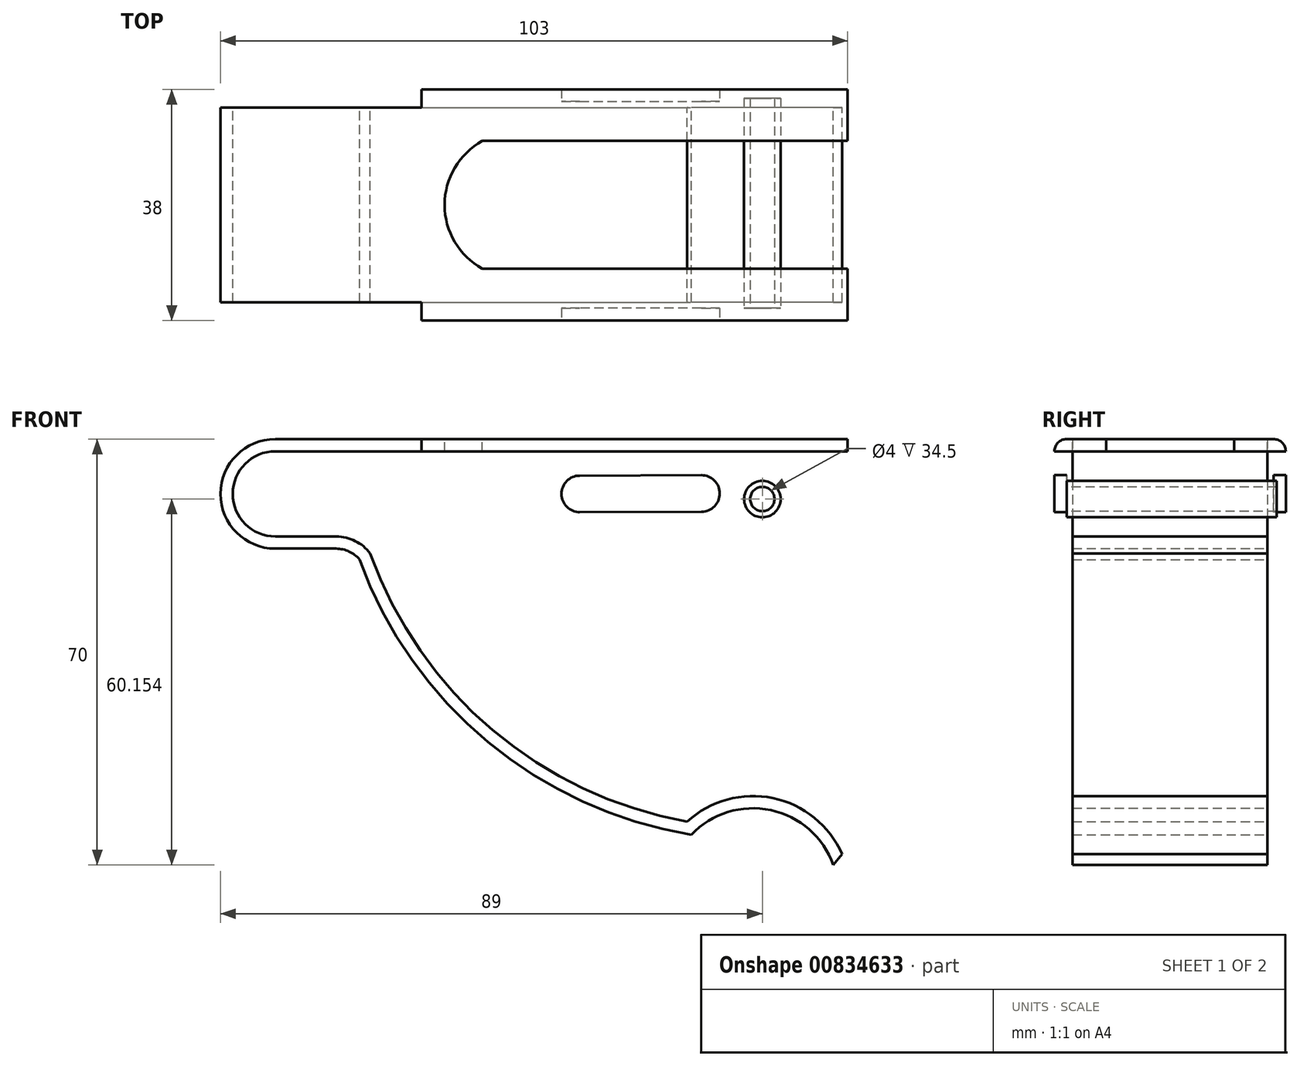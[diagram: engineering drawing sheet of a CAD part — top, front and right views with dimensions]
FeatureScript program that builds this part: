
annotation { "Feature Type Name" : "Feature", "Feature Type Description" : "" }
export const myFeature = defineFeature(function(context is Context, id is Id, definition is map)
    precondition{}
    {
        {
            var Q0;
            Q0=qCreatedBy(makeId("Front.planeOp"),FACE);
            var sketch = newSketch(context, id + "F0", { "sketchPlane" : qUnion([Q0])});
            skArc(sketch, "E0", {"start": v(0, 9) * mm, "mid": v(-9, 0) * mm, "end": v(0, -9) * mm});
            skLineSegment(sketch, "E1", {"start": v(0, 9) * mm, "end": v(94, 9) * mm});
            skLineSegment(sketch, "E2", {"start": v(0, -9) * mm, "end": v(10, -9) * mm});
            skArc(sketch, "E3", {"start": v(13.83, -10.78) * mm, "mid": v(12.1, -9.47) * mm, "end": v(10, -9) * mm});
            skArc(sketch, "E4", {"start": v(13.83, -10.78) * mm, "mid": v(34.94, -40.8) * mm, "end": v(68.33, -56) * mm});
            skArc(sketch, "E5", {"start": v(91.66, -61) * mm, "mid": v(81.4, -51.97) * mm, "end": v(68.33, -56) * mm});
            skLineSegment(sketch, "E6.0", {"start": v(0, 7) * mm, "end": v(94, 7) * mm});
            skArc(sketch, "E6.1", {"start": v(0, 7) * mm, "mid": v(-7, 0) * mm, "end": v(0, -7) * mm});
            skArc(sketch, "E6.2", {"start": v(93.1, -59.22) * mm, "mid": v(81.76, -50) * mm, "end": v(67.66, -53.86) * mm});
            skArc(sketch, "E6.3", {"start": v(15.6, -9.8) * mm, "mid": v(35.7, -38.83) * mm, "end": v(67.66, -53.86) * mm});
            skArc(sketch, "E6.4", {"start": v(15.6, -9.8) * mm, "mid": v(13.13, -7.74) * mm, "end": v(10, -7) * mm});
            skLineSegment(sketch, "E6.5", {"start": v(0, -7) * mm, "end": v(10, -7) * mm});
            skLineSegment(sketch, "E7", {"start": v(91.66, -61) * mm, "end": v(93.1, -59.22) * mm});
            skLineSegment(sketch, "E8", {"start": v(94, 7) * mm, "end": v(94, 9) * mm});
            skSolve(sketch);
        }
        {
            var Q0;
            Q0=makeQuery(id+"F0.imprint","IMPRINT",FACE,{"disambiguationData":[TD([[makeQuery(id+"F0.imprint","IMPRINT",EDGE,{"derivedFrom":sQuery(id+"F0.wireOp",EDGE,"E0")}),1.0]])]});
            extrude(context, id + "F1", {"entities" : qUnion([Q0]), "depth" : 16 * mm, "offsetDistance" : 25 * mm});
        }
        {
            var Q0;
            Q0=makeQuery(id+"F1.opExtrude","SWEPT_FACE",FACE,{"disambiguationData":[OSD([sQuery(id+"F0.wireOp",EDGE,"E1")])]});
            var sketch = newSketch(context, id + "F2", { "sketchPlane" : qUnion([Q0])});
            skLineSegment(sketch, "E9.bottom", {"start": v(94, -16) * mm, "end": v(24, -16) * mm});
            skLineSegment(sketch, "E9.top", {"start": v(94, -19) * mm, "end": v(24, -19) * mm});
            skLineSegment(sketch, "E9.left", {"start": v(94, -16) * mm, "end": v(94, -19) * mm});
            skLineSegment(sketch, "E9.right", {"start": v(24, -16) * mm, "end": v(24, -19) * mm});
            skSolve(sketch);
        }
        {
            var Q0;
            Q0=makeQuery(id+"F2.imprint","IMPRINT",FACE,{"disambiguationData":[TD([[makeQuery(id+"F2.imprint","IMPRINT",EDGE,{"derivedFrom":sQuery(id+"F2.wireOp",EDGE,"E9.bottom")}),-1.0]])]});
            extrude(context, id + "F3", {"entities" : qUnion([Q0]), "operationType" : NewBodyOperationType.ADD, "oppositeDirection" : true, "depth" : 2 * mm, "offsetDistance" : 25 * mm});
        }
        {
            var Q0;
            Q0=makeQuery(id+"F3.opExtrude","SWEPT_FACE",FACE,{"disambiguationData":[OSD([sQuery(id+"F2.wireOp",EDGE,"E9.top")])]});
            var sketch = newSketch(context, id + "F4", { "sketchPlane" : qUnion([Q0])});
            skLineSegment(sketch, "E10.bottom", {"start": v(41.55, 9) * mm, "end": v(94, 9) * mm});
            skLineSegment(sketch, "E10.top", {"start": v(41.55, -6.85) * mm, "end": v(94, -6.85) * mm});
            skLineSegment(sketch, "E10.left", {"start": v(41.55, 9) * mm, "end": v(41.55, -6.85) * mm});
            skLineSegment(sketch, "E10.right", {"start": v(94, 9) * mm, "end": v(94, -6.85) * mm});
            skSolve(sketch);
        }
        {
            var Q0;
            {var subQ0=sQuery(id+"F4.wireOp",EDGE,"E10.top");Q0=makeQuery(id+"F4.imprint","IMPRINT",FACE,{"disambiguationData":[TD([[makeQuery(id+"F4.imprint","IMPRINT",EDGE,{"derivedFrom":subQ0}),1.0]])]});}
            extrude(context, id + "F5", {"entities" : qUnion([Q0]), "operationType" : NewBodyOperationType.ADD, "oppositeDirection" : true, "depth" : 2 * mm, "offsetDistance" : 25 * mm});
        }
        {
            var Q0;
            Q0=makeQuery(id+"F1.opExtrude","SWEPT_BODY",BODY,{"disambiguationData":[OSD([sQuery(id+"F0.wireOp",EDGE,"E0"),sQuery(id+"F0.wireOp",EDGE,"E1"),sQuery(id+"F0.wireOp",EDGE,"E2"),sQuery(id+"F0.wireOp",EDGE,"E3"),sQuery(id+"F0.wireOp",EDGE,"E4"),sQuery(id+"F0.wireOp",EDGE,"E5"),sQuery(id+"F0.wireOp",EDGE,"E6.0"),sQuery(id+"F0.wireOp",EDGE,"E6.1"),sQuery(id+"F0.wireOp",EDGE,"E6.2"),sQuery(id+"F0.wireOp",EDGE,"E6.3"),sQuery(id+"F0.wireOp",EDGE,"E6.4"),sQuery(id+"F0.wireOp",EDGE,"E6.5"),sQuery(id+"F0.wireOp",EDGE,"E7"),sQuery(id+"F0.wireOp",EDGE,"E8")])]});
            var Q1;
            Q1=makeQuery(id+"F1.opExtrude","CAP_FACE",FACE,{"disambiguationData":[OSD([sQuery(id+"F0.wireOp",EDGE,"E0"),sQuery(id+"F0.wireOp",EDGE,"E1"),sQuery(id+"F0.wireOp",EDGE,"E2"),sQuery(id+"F0.wireOp",EDGE,"E3"),sQuery(id+"F0.wireOp",EDGE,"E4"),sQuery(id+"F0.wireOp",EDGE,"E5"),sQuery(id+"F0.wireOp",EDGE,"E6.0"),sQuery(id+"F0.wireOp",EDGE,"E6.1"),sQuery(id+"F0.wireOp",EDGE,"E6.2"),sQuery(id+"F0.wireOp",EDGE,"E6.3"),sQuery(id+"F0.wireOp",EDGE,"E6.4"),sQuery(id+"F0.wireOp",EDGE,"E6.5"),sQuery(id+"F0.wireOp",EDGE,"E7"),sQuery(id+"F0.wireOp",EDGE,"E8")])],"isStart":true});
            mirror(context, id + "F6", {"operationType" : NewBodyOperationType.ADD, "entities" : qUnion([Q0]), "mirrorPlane" : qUnion([Q1])});
        }
        {
            var Q0;
            {var subQ0=makeQuery(id+"F3.boolean.opBoolean","MERGE",FACE,{"derivedFrom":[makeQuery(id+"F1.opExtrude","SWEPT_FACE",FACE,{"disambiguationData":[OSD([sQuery(id+"F0.wireOp",EDGE,"E1")])]}),makeQuery(id+"F3.opExtrude","CAP_FACE",FACE,{"disambiguationData":[OSD([sQuery(id+"F2.wireOp",EDGE,"E9.bottom"),sQuery(id+"F2.wireOp",EDGE,"E9.top"),sQuery(id+"F2.wireOp",EDGE,"E9.left"),sQuery(id+"F2.wireOp",EDGE,"E9.right")])],"isStart":true})]});Q0=makeQuery(id+"F6.boolean.opBoolean","MERGE",FACE,{"derivedFrom":[subQ0,makeQuery(id+"F6.opPattern","COPY",FACE,{"derivedFrom":subQ0,"instanceName":"1"})]});}
            var sketch = newSketch(context, id + "F7", { "sketchPlane" : qUnion([Q0])});
            skLineSegment(sketch, "E11", {"start": v(94, -10.5) * mm, "end": v(34, -10.5) * mm});
            skLineSegment(sketch, "E12", {"start": v(94, 10.5) * mm, "end": v(34, 10.5) * mm});
            skArc(sketch, "E13", {"start": v(34, 10.5) * mm, "mid": v(27.8, 0) * mm, "end": v(34, -10.5) * mm});
            skSolve(sketch);
        }
        {
            var Q0;
            {var subQ0=sQuery(id+"F7.wireOp",EDGE,"E11");Q0=makeQuery(id+"F7.imprint","IMPRINT",FACE,{"disambiguationData":[TD([[makeQuery(id+"F7.imprint","IMPRINT",EDGE,{"derivedFrom":subQ0}),-1.0]])]});}
            extrude(context, id + "F8", {"entities" : qUnion([Q0]), "operationType" : NewBodyOperationType.REMOVE, "oppositeDirection" : true, "depth" : 2 * mm, "offsetDistance" : 25 * mm});
        }
        {
            var Q0;
            Q0=makeQuery(id+"F3.opExtrude","CAP_EDGE",EDGE,{"disambiguationData":[OSD([sQuery(id+"F2.wireOp",EDGE,"E9.top")])],"isStart":true});
            var Q1;
            Q1=makeQuery(id+"F6.opPattern","COPY",EDGE,{"derivedFrom":makeQuery(id+"F3.opExtrude","CAP_EDGE",EDGE,{"disambiguationData":[OSD([sQuery(id+"F2.wireOp",EDGE,"E9.top")])],"isStart":true}),"instanceName":"1"});
            fillet(context, id + "F9", {"entities" : qUnion([Q0, Q1]), "radius" : 2 * mm, "tangentPropagation" : true, "allowEdgeOverflow" : false});
        }
        {
            var Q0;
            {var subQ0=sQuery(id+"F2.wireOp",EDGE,"E9.top");Q0=makeQuery(id+"F5.boolean.opBoolean","MERGE",FACE,{"derivedFrom":[makeQuery(id+"F3.opExtrude","SWEPT_FACE",FACE,{"disambiguationData":[OSD([subQ0])]}),makeQuery(id+"F5.opExtrude","CAP_FACE",FACE,{"disambiguationData":[OSD([subQ0,sQuery(id+"F4.wireOp",EDGE,"E10.top"),sQuery(id+"F4.wireOp",EDGE,"E10.left"),sQuery(id+"F4.wireOp",EDGE,"E10.right")])],"isStart":true})]});}
            var sketch = newSketch(context, id + "F10", { "sketchPlane" : qUnion([Q0])});
            skLineSegment(sketch, "E14", {"start": v(70, 0.08) * mm, "end": v(50, 0) * mm});
            skPoint(sketch, "E14.startSnap0", {"position": v(41.55, 0.08) * mm});
            skArc(sketch, "E15.0.startCap", {"start": v(69.99, 3.08) * mm, "mid": v(73, 0.09) * mm, "end": v(70.01, -2.92) * mm});
            skArc(sketch, "E15.0.endCap", {"start": v(50.01, -3) * mm, "mid": v(47, -0.01) * mm, "end": v(49.99, 3) * mm});
            skLineSegment(sketch, "E15.0.left", {"start": v(70.01, -2.92) * mm, "end": v(50.01, -3) * mm});
            skLineSegment(sketch, "E15.0.right", {"start": v(69.99, 3.08) * mm, "end": v(49.99, 3) * mm});
            skSolve(sketch);
        }
        {
            var Q0;
            Q0=makeQuery(id+"F10.imprint","IMPRINT",FACE,{"disambiguationData":[TD([[makeQuery(id+"F10.imprint","IMPRINT",EDGE,{"derivedFrom":sQuery(id+"F10.wireOp",EDGE,"E15.0.startCap")}),-1.0]])]});
            extrude(context, id + "F11", {"entities" : qUnion([Q0]), "operationType" : NewBodyOperationType.REMOVE, "endBound" : BoundingType.THROUGH_ALL, "oppositeDirection" : true, "depth" : 54.5 * mm, "offsetDistance" : 25 * mm});
        }
        {
            var Q0;
            {var subQ0=sQuery(id+"F2.wireOp",EDGE,"E9.top");Q0=makeQuery(id+"F6.opPattern","COPY",FACE,{"derivedFrom":makeQuery(id+"F5.boolean.opBoolean","MERGE",FACE,{"derivedFrom":[makeQuery(id+"F3.opExtrude","SWEPT_FACE",FACE,{"disambiguationData":[OSD([subQ0])]}),makeQuery(id+"F5.opExtrude","CAP_FACE",FACE,{"disambiguationData":[OSD([subQ0,sQuery(id+"F4.wireOp",EDGE,"E10.top"),sQuery(id+"F4.wireOp",EDGE,"E10.left"),sQuery(id+"F4.wireOp",EDGE,"E10.right")])],"isStart":true})]}),"instanceName":"1"});}
            var sketch = newSketch(context, id + "F12", { "sketchPlane" : qUnion([Q0])});
            skPoint(sketch, "E16", {"position": v(-80, -0.85) * mm});
            skSolve(sketch);
        }
        {
            var Q0;
            Q0=sQuery(id+"F12.wireOp",VERTEX,"E16");
            var Q1;
            Q1=makeQuery(id+"F1.opExtrude","SWEPT_BODY",BODY,{"disambiguationData":[OSD([sQuery(id+"F0.wireOp",EDGE,"E0"),sQuery(id+"F0.wireOp",EDGE,"E1"),sQuery(id+"F0.wireOp",EDGE,"E2"),sQuery(id+"F0.wireOp",EDGE,"E3"),sQuery(id+"F0.wireOp",EDGE,"E4"),sQuery(id+"F0.wireOp",EDGE,"E5"),sQuery(id+"F0.wireOp",EDGE,"E6.0"),sQuery(id+"F0.wireOp",EDGE,"E6.1"),sQuery(id+"F0.wireOp",EDGE,"E6.2"),sQuery(id+"F0.wireOp",EDGE,"E6.3"),sQuery(id+"F0.wireOp",EDGE,"E6.4"),sQuery(id+"F0.wireOp",EDGE,"E6.5"),sQuery(id+"F0.wireOp",EDGE,"E7"),sQuery(id+"F0.wireOp",EDGE,"E8")])]});
            hole(context, id + "F13", {"style" : HoleStyle.SIMPLE, "endStyle" : HoleEndStyle.THROUGH, "holeDiameter" : 4 * mm, "majorDiameter" : 5 * mm, "isTappedThrough" : true, "tappedDepth" : 12 * mm, "tapClearance" : 3, "locations" : qUnion([Q0]), "scope" : qUnion([Q1])});
        }
        {
            var Q0;
            Q0=makeQuery(id+"F5.opExtrude","CAP_FACE",FACE,{"disambiguationData":[OSD([sQuery(id+"F2.wireOp",EDGE,"E9.top"),sQuery(id+"F4.wireOp",EDGE,"E10.top"),sQuery(id+"F4.wireOp",EDGE,"E10.left"),sQuery(id+"F4.wireOp",EDGE,"E10.right")])],"isStart":false});
            var sketch = newSketch(context, id + "F14", { "sketchPlane" : qUnion([Q0])});
            skCircle(sketch, "E17.0", {"center": v(-80, -0.85) * mm, "radius": 2 * mm});
            skLineSegment(sketch, "E18.0.0", {"start": v(-94, 7) * mm, "end": v(-94, -6.85) * mm});
            skLineSegment(sketch, "E18.0.1", {"start": v(-94, -6.85) * mm, "end": v(-41.55, -6.85) * mm});
            skLineSegment(sketch, "E18.0.2", {"start": v(-41.55, -6.85) * mm, "end": v(-41.55, 7) * mm});
            skLineSegment(sketch, "E18.0.3", {"start": v(-41.55, 7) * mm, "end": v(-94, 7) * mm});
            skCircle(sketch, "E19.0", {"center": v(-80, -0.85) * mm, "radius": 3 * mm});
            skLineSegment(sketch, "E20.0", {"start": v(-99, 12) * mm, "end": v(-99, -11.85) * mm});
            skLineSegment(sketch, "E20.1", {"start": v(-36.55, 12) * mm, "end": v(-99, 12) * mm});
            skLineSegment(sketch, "E20.2", {"start": v(-36.55, -11.85) * mm, "end": v(-36.55, 12) * mm});
            skLineSegment(sketch, "E20.3", {"start": v(-99, -11.85) * mm, "end": v(-36.55, -11.85) * mm});
            skSolve(sketch);
        }
        {
            var Q0;
            Q0=makeQuery(id+"F14.imprint","IMPRINT",FACE,{"disambiguationData":[TD([[makeQuery(id+"F14.imprint","IMPRINT",EDGE,{"derivedFrom":sQuery(id+"F14.wireOp",EDGE,"E17.0")}),-1.0]])]});
            extrude(context, id + "F15", {"entities" : qUnion([Q0]), "operationType" : NewBodyOperationType.ADD, "depth" : 34.5 * mm, "offsetDistance" : 25 * mm});
        }
    });
